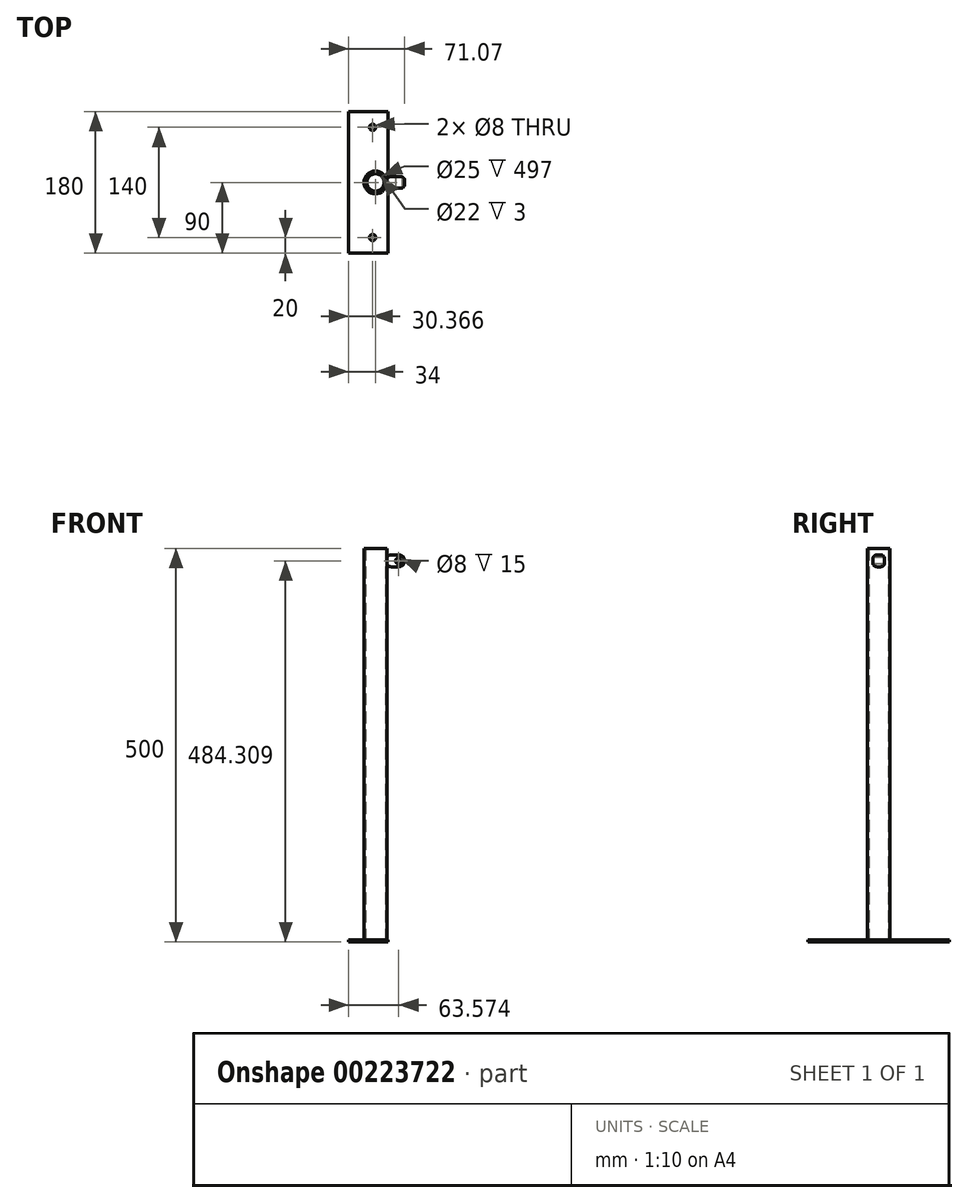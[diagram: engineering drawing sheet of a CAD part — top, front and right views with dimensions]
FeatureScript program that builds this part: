
annotation { "Feature Type Name" : "Feature", "Feature Type Description" : "" }
export const myFeature = defineFeature(function(context is Context, id is Id, definition is map)
    precondition{}
    {
        {
            var Q0;
            Q0=qCreatedBy(makeId("Top.planeOp"),FACE);
            var sketch = newSketch(context, id + "F0", { "sketchPlane" : qUnion([Q0])});
            skCircle(sketch, "E0", {"center": v(0, 0) * mm, "radius": 14.5 * mm});
            skCircle(sketch, "E1", {"center": v(0, 0) * mm, "radius": 12.5 * mm});
            skSolve(sketch);
        }
        {
            var Q0;
            Q0=qSketchRegion(id+"F0",true);
            extrude(context, id + "F1", {"entities" : qUnion([Q0]), "depth" : 500 * mm});
        }
        {
            var Q0;
            Q0=qCreatedBy(makeId("Top.planeOp"),FACE);
            var sketch = newSketch(context, id + "F2", { "sketchPlane" : qUnion([Q0])});
            skLineSegment(sketch, "E2", {"start": v(16, 0) * mm, "end": v(16, 90) * mm});
            skLineSegment(sketch, "E3", {"start": v(16, 90) * mm, "end": v(-34, 90) * mm});
            skLineSegment(sketch, "E4", {"start": v(-34, 90) * mm, "end": v(-34, -90) * mm});
            skLineSegment(sketch, "E5", {"start": v(-34, -90) * mm, "end": v(16, -90) * mm});
            skLineSegment(sketch, "E6", {"start": v(16, -90) * mm, "end": v(16, 0) * mm});
            skCircle(sketch, "E7", {"center": v(0, 0) * mm, "radius": 11 * mm});
            skCircle(sketch, "E8", {"center": v(-3.63, -70) * mm, "radius": 4 * mm});
            skCircle(sketch, "E9", {"center": v(-3.63, 70) * mm, "radius": 4 * mm});
            skSolve(sketch);
        }
        {
            var Q0;
            Q0=qSketchRegion(id+"F2",true);
            extrude(context, id + "F3", {"entities" : qUnion([Q0]), "operationType" : NewBodyOperationType.ADD, "depth" : 3 * mm});
        }
        {
            var Q0;
            Q0=qCreatedBy(makeId("Front.planeOp"),FACE);
            var sketch = newSketch(context, id + "F4", { "sketchPlane" : qUnion([Q0])});
            skLineSegment(sketch, "E10", {"start": v(14.57, 491.8) * mm, "end": v(14.57, 476.8) * mm});
            skLineSegment(sketch, "E11", {"start": v(14.57, 476.8) * mm, "end": v(29.57, 476.8) * mm});
            skLineSegment(sketch, "E12", {"start": v(29.57, 476.8) * mm, "end": v(29.57, 491.8) * mm});
            skLineSegment(sketch, "E13", {"start": v(29.57, 491.8) * mm, "end": v(14.57, 491.8) * mm});
            skArc(sketch, "E14", {"start": v(29.57, 491.8) * mm, "mid": v(37.07, 484.3) * mm, "end": v(29.57, 476.8) * mm});
            skSolve(sketch);
        }
        {
            var Q0;
            Q0=qSketchRegion(id+"F4",true);
            extrude(context, id + "F5", {"entities" : qUnion([Q0]), "endBound" : BoundingType.SYMMETRIC, "depth" : 15 * mm});
        }
        {
            var Q0;
            Q0=makeQuery(id+"F5.opExtrude","CAP_EDGE",EDGE,{"disambiguationData":[OSD([sQuery(id+"F4.wireOp",EDGE,"E10")])],"isStart":false});
            var Q1;
            Q1=makeQuery(id+"F5.opExtrude","CAP_EDGE",EDGE,{"disambiguationData":[OSD([sQuery(id+"F4.wireOp",EDGE,"E14")])],"isStart":false});
            var Q2;
            Q2=makeQuery(id+"F5.opExtrude","CAP_EDGE",EDGE,{"disambiguationData":[OSD([sQuery(id+"F4.wireOp",EDGE,"E11")])],"isStart":true});
            fillet(context, id + "F6", {"entities" : qUnion([Q0, Q1, Q2]), "radius" : 5 * mm, "tangentPropagation" : true, "allowEdgeOverflow" : false});
        }
        {
            var Q0;
            Q0=makeQuery(id+"F5.opExtrude","CAP_EDGE",EDGE,{"disambiguationData":[OSD([sQuery(id+"F4.wireOp",EDGE,"E10")])],"isStart":true});
            fillet(context, id + "F7", {"entities" : qUnion([Q0]), "radius" : 5 * mm, "tangentPropagation" : true, "allowEdgeOverflow" : false});
        }
        {
            var Q0;
            Q0=makeQuery(id+"F5.opExtrude","CAP_FACE",FACE,{"disambiguationData":[OSD([sQuery(id+"F4.wireOp",EDGE,"E10"),sQuery(id+"F4.wireOp",EDGE,"E11"),sQuery(id+"F4.wireOp",EDGE,"E13"),sQuery(id+"F4.wireOp",EDGE,"E14")])],"isStart":false});
            var sketch = newSketch(context, id + "F8", { "sketchPlane" : qUnion([Q0])});
            skPoint(sketch, "E15", {"position": v(29.57, 484.3) * mm});
            skSolve(sketch);
        }
        {
            var Q0;
            Q0=sQuery(id+"F8.wireOp",VERTEX,"E15");
            var Q1;
            Q1=makeQuery(id+"F5.opExtrude","SWEPT_BODY",BODY,{"disambiguationData":[OSD([sQuery(id+"F4.wireOp",EDGE,"E10"),sQuery(id+"F4.wireOp",EDGE,"E11"),sQuery(id+"F4.wireOp",EDGE,"E13"),sQuery(id+"F4.wireOp",EDGE,"E14")])]});
            hole(context, id + "F9", {"style" : HoleStyle.SIMPLE, "endStyle" : HoleEndStyle.THROUGH, "holeDiameter" : 8 * mm, "startFromSketch" : true, "locations" : qUnion([Q0]), "scope" : qUnion([Q1]), "isTappedThrough" : true});
        }
    });
